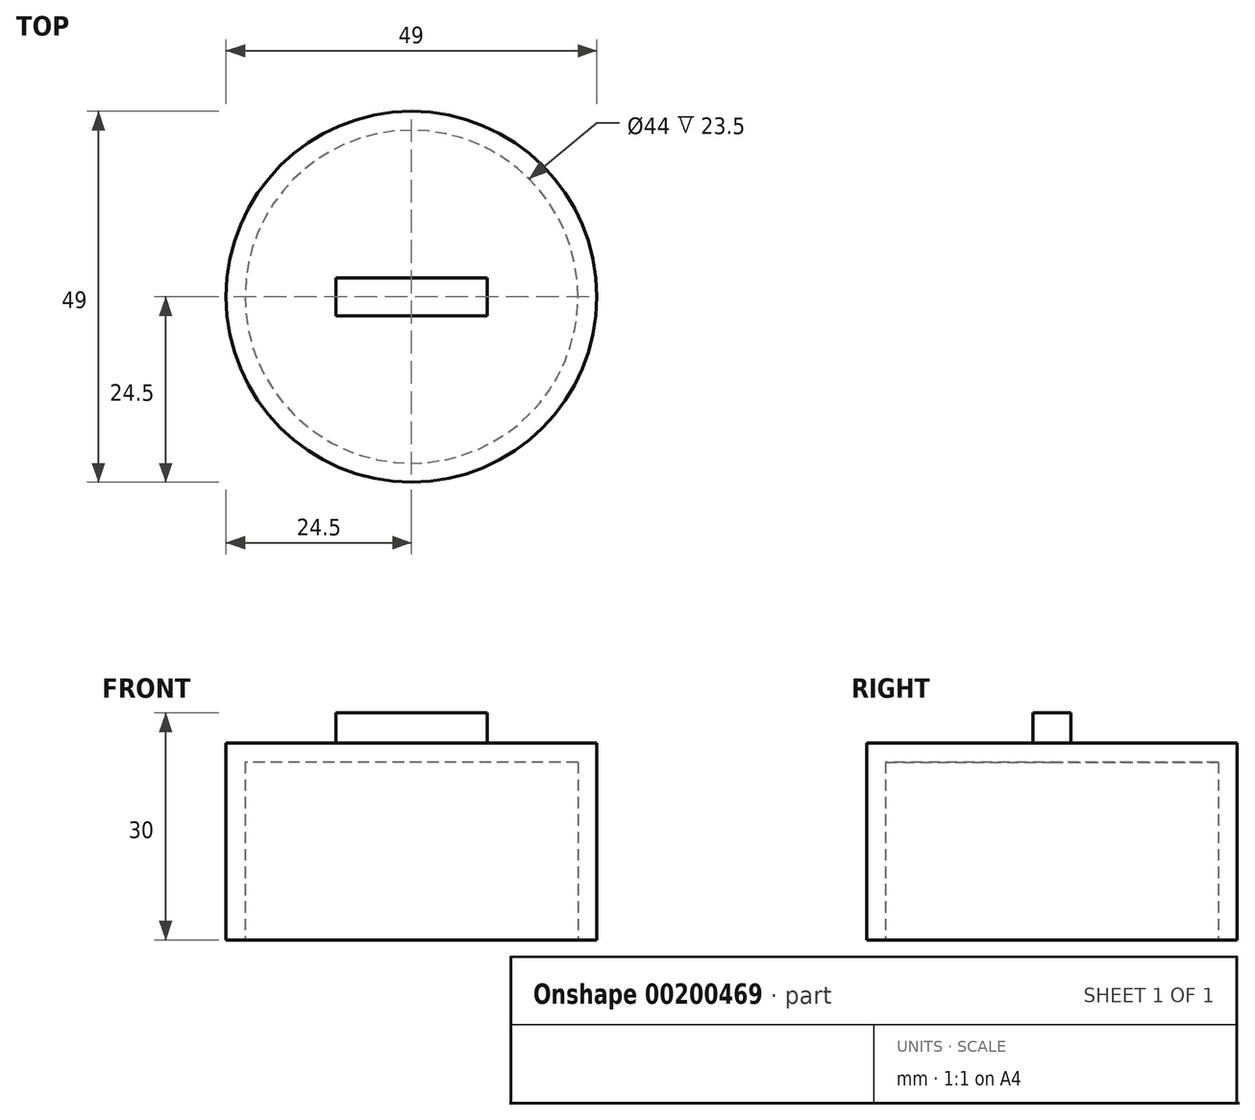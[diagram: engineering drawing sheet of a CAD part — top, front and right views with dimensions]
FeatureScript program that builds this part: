
annotation { "Feature Type Name" : "Feature", "Feature Type Description" : "" }
export const myFeature = defineFeature(function(context is Context, id is Id, definition is map)
    precondition{}
    {
        {
            var Q0;
            Q0=qCreatedBy(makeId("Top.planeOp"),FACE);
            var sketch = newSketch(context, id + "F0", { "sketchPlane" : qUnion([Q0])});
            skCircle(sketch, "E0", {"center": v(0, 0) * mm, "radius": 24.5 * mm});
            skSolve(sketch);
        }
        {
            var Q0;
            Q0 = qSketchRegion(id + "F0", true);
            extrude(context, id + "F1", {"entities" : qUnion([Q0]), "depth" : 26 * mm});
        }
        {
            var Q0;
            Q0=makeQuery(id+"F1.opExtrude","CAP_FACE",FACE,{"disambiguationData":[OSD([sQuery(id+"F0.wireOp",EDGE,"E0")])],"isStart":true});
            shell(context, id + "F2", {"entities" : qUnion([Q0]), "thickness" : 2.5 * mm});
        }
        {
            var Q0;
            Q0=makeQuery(id+"F1.opExtrude","CAP_FACE",FACE,{"disambiguationData":[OSD([sQuery(id+"F0.wireOp",EDGE,"E0")])],"isStart":false});
            var sketch = newSketch(context, id + "F3", { "sketchPlane" : qUnion([Q0])});
            skLineSegment(sketch, "E1.bottom", {"start": v(-10, 2.5) * mm, "end": v(10, 2.5) * mm});
            skLineSegment(sketch, "E1.top", {"start": v(-10, -2.5) * mm, "end": v(10, -2.5) * mm});
            skLineSegment(sketch, "E1.left", {"start": v(-10, 2.5) * mm, "end": v(-10, -2.5) * mm});
            skLineSegment(sketch, "E1.right", {"start": v(10, 2.5) * mm, "end": v(10, -2.5) * mm});
            skPoint(sketch, "E1.middle", {"position": v(0, 0) * mm});
            skSolve(sketch);
        }
        {
            var Q0;
            Q0 = qSketchRegion(id + "F3", true);
            extrude(context, id + "F4", {"entities" : qUnion([Q0]), "operationType" : NewBodyOperationType.ADD, "depth" : 4 * mm});
        }
    });
